# Revit family: ETA-16-0262.K.007.50 Kontrollankerkopf (K) temp L7
name_source: partatom
category: Allgemeines Modell
units: mm (PartAtom-declared; Revit-internal decimal feet)

## family parameters
Arbeitsebenenbasiert = Nein
Beim Laden mit Abzugskörper schneiden = Nein
Bemaßung runder Anschluss = Durchmesser verwenden
Gemeinsam genutzt = Nein
Immer vertikal = Ja
Kann Basisbauteil für Bewehrung sein = Nein
Raumberechnungspunkt = Nein
Teiletyp = Normal

## types (1)
- Norm
    11 Title German = Kontrollankerkopf (K) temp L7
    12 Title Englisch = control anchor head (K) , temp.
    14 Zeichnungsnummer = ETA-16-0262.K.007.50
    Bauteilnummer = ETA-16-0262.K.007.50 Kontrollankerkopf (K) temp L7
    Beschreibung = Kontrollanker temp  L7
    Erstellungsdatum = 14.05.2024 00:00:00
    Hersteller = BBV-Systems
    Modell = ETA-16-0262.K.007.50.0
    Vorgabe-Ansicht = 0 mm  [stored 0 ft]

note: [stored X ft] marks values corroborated as IEEE doubles in the binary element streams (Revit-internal decimal feet)
